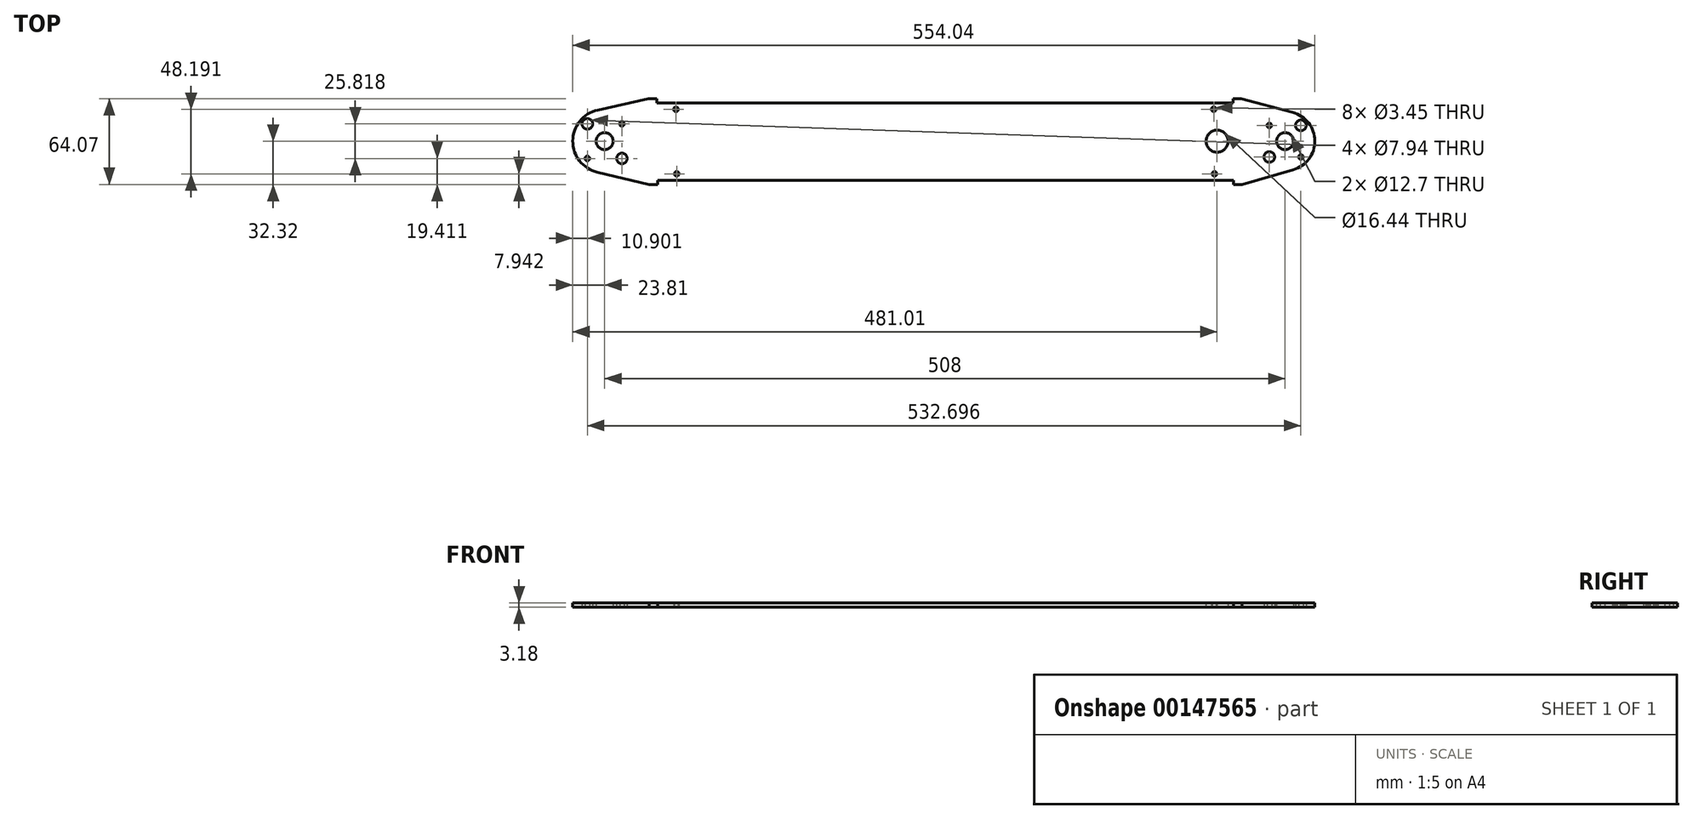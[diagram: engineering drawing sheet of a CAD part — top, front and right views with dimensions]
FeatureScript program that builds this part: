
annotation { "Feature Type Name" : "Feature", "Feature Type Description" : "" }
export const myFeature = defineFeature(function(context is Context, id is Id, definition is map)
    precondition{}
    {
        {
            var Q0;
            Q0=qCreatedBy(makeId("Top.planeOp"),FACE);
            var sketch = newSketch(context, id + "F0", { "sketchPlane" : qUnion([Q0])});
            skPoint(sketch, "E0.rect.middle", {"position": v(0, 0) * mm});
            skCircle(sketch, "E1", {"center": v(0, 0) * mm, "radius": 11.11 * mm, "construction": true});
            skLineSegment(sketch, "E2.bottom", {"start": v(11.79, 11.79) * mm, "end": v(-11.79, 11.79) * mm, "construction": true});
            skLineSegment(sketch, "E2.left", {"start": v(11.79, 11.79) * mm, "end": v(11.79, -11.79) * mm, "construction": true});
            skLineSegment(sketch, "E2.right", {"start": v(-11.79, 11.79) * mm, "end": v(-11.79, -11.79) * mm, "construction": true});
            skCircle(sketch, "E3", {"center": v(11.79, 11.79) * mm, "radius": 5.56 * mm, "construction": true});
            skCircle(sketch, "E4", {"center": v(-11.79, 11.79) * mm, "radius": 1.73 * mm});
            skCircle(sketch, "E5", {"center": v(11.79, 11.79) * mm, "radius": 3.97 * mm});
            skCircle(sketch, "E6", {"center": v(11.79, -11.79) * mm, "radius": 1.73 * mm});
            skCircle(sketch, "E7", {"center": v(-11.79, -11.79) * mm, "radius": 3.97 * mm});
            skArc(sketch, "E8", {"start": v(-513.23, 23.23) * mm, "mid": v(-531.81, 0.13) * mm, "end": v(-513.48, -23.17) * mm});
            skLineSegment(sketch, "E9.bottom", {"start": v(-520.9, 12.9) * mm, "end": v(-495.1, 12.9) * mm, "construction": true});
            skLineSegment(sketch, "E9.top", {"start": v(-520.9, -12.9) * mm, "end": v(-495.1, -12.9) * mm, "construction": true});
            skLineSegment(sketch, "E9.left", {"start": v(-520.9, 12.9) * mm, "end": v(-520.9, -12.9) * mm, "construction": true});
            skLineSegment(sketch, "E9.right", {"start": v(-495.1, 12.9) * mm, "end": v(-495.1, -12.9) * mm, "construction": true});
            skCircle(sketch, "E10", {"center": v(-495.1, 12.9) * mm, "radius": 1.73 * mm});
            skCircle(sketch, "E11", {"center": v(-508, 0) * mm, "radius": 6.35 * mm});
            skCircle(sketch, "E12", {"center": v(-520.9, 12.9) * mm, "radius": 3.97 * mm});
            skCircle(sketch, "E13", {"center": v(-520.9, -12.9) * mm, "radius": 1.73 * mm});
            skCircle(sketch, "E14", {"center": v(-495.1, -12.9) * mm, "radius": 3.97 * mm});
            skLineSegment(sketch, "E15", {"start": v(0, 0) * mm, "end": v(-508, 0) * mm, "construction": true});
            skLineSegment(sketch, "E16", {"start": v(-513.48, -23.17) * mm, "end": v(-474.82, -32.32) * mm});
            skLineSegment(sketch, "E17", {"start": v(-513.23, 23.23) * mm, "end": v(-475.38, 31.75) * mm});
            skLineSegment(sketch, "E18", {"start": v(-468.47, -29.14) * mm, "end": v(-38.41, -29.14) * mm});
            skLineSegment(sketch, "E19", {"start": v(-469.03, 28.57) * mm, "end": v(-38.97, 28.57) * mm});
            skLineSegment(sketch, "E20", {"start": v(-469.03, 31.75) * mm, "end": v(-469.03, 28.57) * mm});
            skLineSegment(sketch, "E21", {"start": v(-469.03, 31.75) * mm, "end": v(-475.38, 31.75) * mm});
            skLineSegment(sketch, "E22", {"start": v(-468.47, -29.14) * mm, "end": v(-468.47, -32.32) * mm});
            skLineSegment(sketch, "E23", {"start": v(-468.47, -32.32) * mm, "end": v(-474.82, -32.32) * mm});
            skLineSegment(sketch, "E24", {"start": v(-38.41, -29.14) * mm, "end": v(-38.41, -32.32) * mm});
            skLineSegment(sketch, "E25", {"start": v(-38.41, -32.32) * mm, "end": v(-32.06, -32.32) * mm});
            skLineSegment(sketch, "E26", {"start": v(-38.97, 28.57) * mm, "end": v(-38.97, 31.75) * mm});
            skLineSegment(sketch, "E27", {"start": v(-38.97, 31.75) * mm, "end": v(-32.62, 31.75) * mm});
            skLineSegment(sketch, "E28", {"start": v(-32.06, -32.32) * mm, "end": v(6.13, -21.36) * mm});
            skLineSegment(sketch, "E29", {"start": v(5.75, 21.47) * mm, "end": v(-32.62, 31.75) * mm});
            skArc(sketch, "E30", {"start": v(6.13, -21.36) * mm, "mid": v(22.22, 0.2) * mm, "end": v(5.75, 21.47) * mm});
            skLineSegment(sketch, "E31", {"start": v(-469.03, 28.57) * mm, "end": v(-469.03, 23.81) * mm, "construction": true});
            skLineSegment(sketch, "E32", {"start": v(-469.03, 23.81) * mm, "end": v(-454.74, 23.81) * mm, "construction": true});
            skLineSegment(sketch, "E33", {"start": v(-468.47, -29.14) * mm, "end": v(-468.47, -24.38) * mm, "construction": true});
            skLineSegment(sketch, "E34", {"start": v(-468.47, -24.38) * mm, "end": v(-454.18, -24.38) * mm, "construction": true});
            skLineSegment(sketch, "E35", {"start": v(-38.41, -29.14) * mm, "end": v(-38.41, -24.38) * mm, "construction": true});
            skLineSegment(sketch, "E36", {"start": v(-38.41, -24.38) * mm, "end": v(-52.7, -24.38) * mm, "construction": true});
            skLineSegment(sketch, "E37", {"start": v(-38.97, 28.57) * mm, "end": v(-38.97, 23.81) * mm, "construction": true});
            skLineSegment(sketch, "E38", {"start": v(-38.97, 23.81) * mm, "end": v(-53.26, 23.81) * mm, "construction": true});
            skCircle(sketch, "E39", {"center": v(-454.74, 23.81) * mm, "radius": 1.73 * mm});
            skCircle(sketch, "E40", {"center": v(-53.26, 23.81) * mm, "radius": 1.73 * mm});
            skCircle(sketch, "E41", {"center": v(-52.7, -24.38) * mm, "radius": 1.73 * mm});
            skCircle(sketch, "E42", {"center": v(-454.18, -24.38) * mm, "radius": 1.73 * mm});
            skLineSegment(sketch, "E43", {"start": v(-11.79, -11.79) * mm, "end": v(11.79, -11.79) * mm, "construction": true});
            skLineSegment(sketch, "E44", {"start": v(-254, -28.58) * mm, "end": v(-254, 0) * mm, "construction": true});
            skLineSegment(sketch, "E45", {"start": v(-254, 0) * mm, "end": v(-254, 28.58) * mm, "construction": true});
            skLineSegment(sketch, "E46", {"start": v(-11.79, 11.79) * mm, "end": v(-50.8, 11.79) * mm, "construction": true});
            skLineSegment(sketch, "E47", {"start": v(-50.8, 11.79) * mm, "end": v(-50.8, 0) * mm, "construction": true});
            skCircle(sketch, "E48", {"center": v(-50.8, 0) * mm, "radius": 8.22 * mm});
            skCircle(sketch, "E49", {"center": v(-520.9, -12.9) * mm, "radius": 5.56 * mm, "construction": true});
            skCircle(sketch, "E50", {"center": v(0, 0) * mm, "radius": 6.35 * mm});
            skSolve(sketch);
        }
        {
            var Q0;
            Q0=qSketchRegion(id+"F0",true);
            extrude(context, id + "F1", {"entities" : qUnion([Q0]), "depth" : 3.17 * mm});
        }
    });
